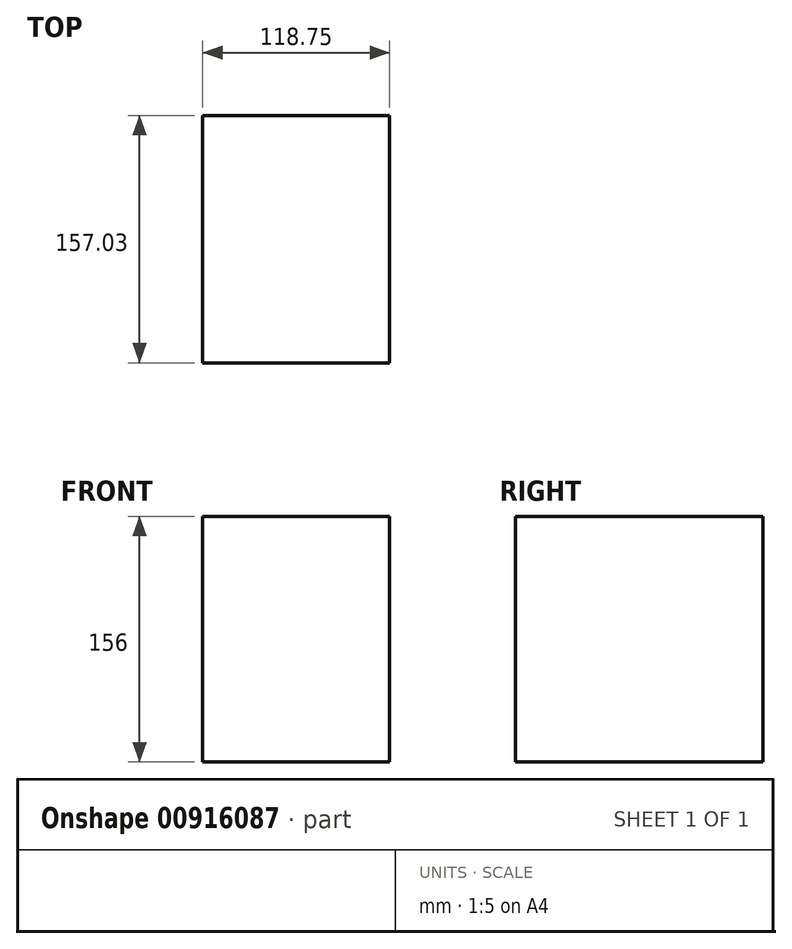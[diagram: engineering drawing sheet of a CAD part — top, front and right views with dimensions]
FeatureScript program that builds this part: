
annotation { "Feature Type Name" : "Feature", "Feature Type Description" : "" }
export const myFeature = defineFeature(function(context is Context, id is Id, definition is map)
    precondition{}
    {
        {
            var Q0;
            Q0=qCreatedBy(makeId("Top.planeOp"),FACE);
            var sketch = newSketch(context, id + "F0", { "sketchPlane" : qUnion([Q0])});
            skLineSegment(sketch, "E0.bottom", {"start": v(65.76, 93.8) * mm, "end": v(-52.99, 93.8) * mm});
            skLineSegment(sketch, "E0.top", {"start": v(65.76, -63.23) * mm, "end": v(-52.99, -63.23) * mm});
            skLineSegment(sketch, "E0.left", {"start": v(65.76, 93.8) * mm, "end": v(65.76, -63.23) * mm});
            skLineSegment(sketch, "E0.right", {"start": v(-52.99, 93.8) * mm, "end": v(-52.99, -63.23) * mm});
            skSolve(sketch);
        }
        {
            var Q0;
            Q0=makeQuery(id+"F0.imprint","IMPRINT",FACE,{"disambiguationData":[TD([[makeQuery(id+"F0.imprint","IMPRINT",EDGE,{"derivedFrom":sQuery(id+"F0.wireOp",EDGE,"E0.bottom")}),1.0]])]});
            extrude(context, id + "F1", {"entities" : qUnion([Q0]), "depth" : 156 * mm, "offsetDistance" : 25 * mm});
        }
    });
